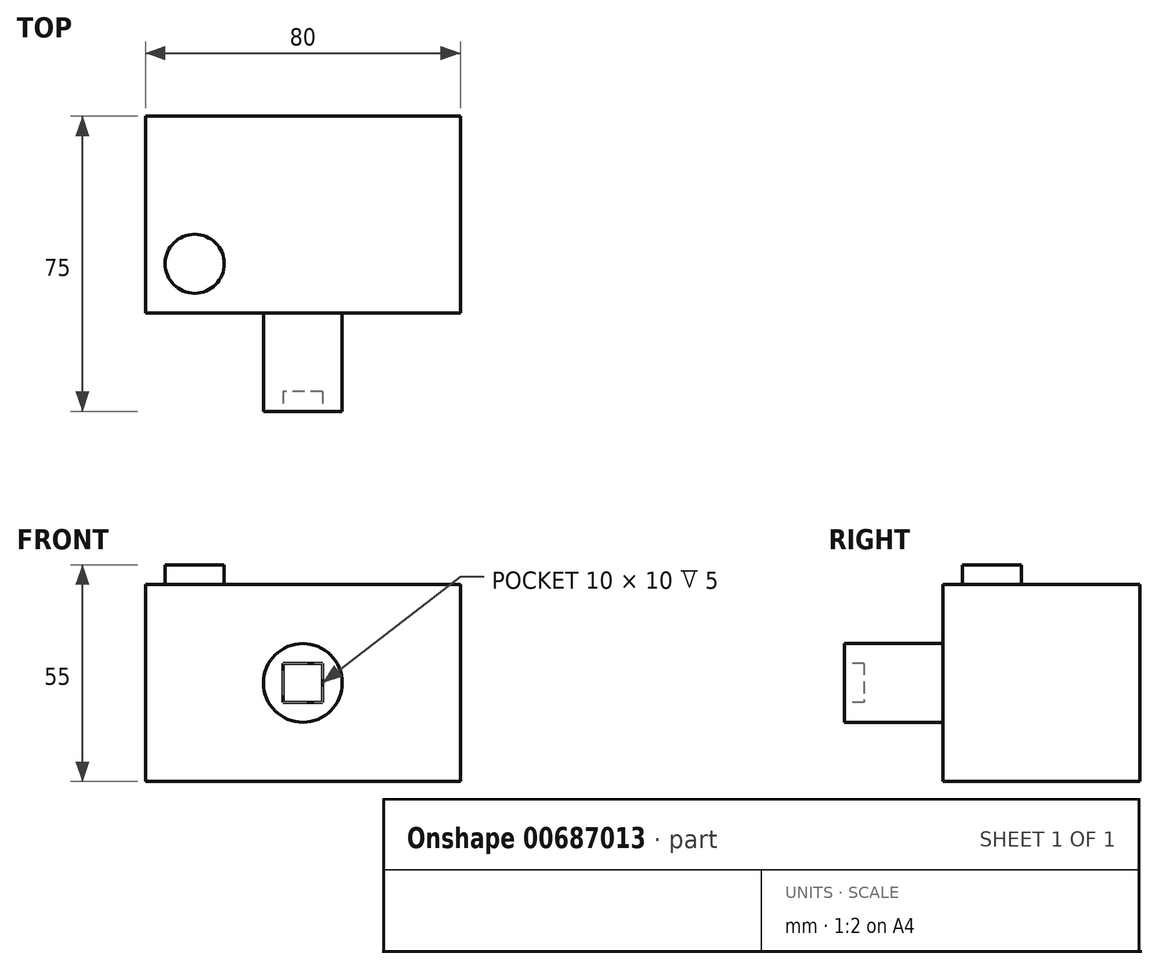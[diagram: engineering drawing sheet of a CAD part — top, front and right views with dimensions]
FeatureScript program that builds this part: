
annotation { "Feature Type Name" : "Feature", "Feature Type Description" : "" }
export const myFeature = defineFeature(function(context is Context, id is Id, definition is map)
    precondition{}
    {
        {
            var Q0;
            Q0=qCreatedBy(makeId("Top.planeOp"),FACE);
            var sketch = newSketch(context, id + "F0", { "sketchPlane" : qUnion([Q0])});
            skLineSegment(sketch, "E0.bottom", {"start": v(40, 25) * mm, "end": v(-40, 25) * mm});
            skLineSegment(sketch, "E0.top", {"start": v(40, -25) * mm, "end": v(-40, -25) * mm});
            skLineSegment(sketch, "E0.left", {"start": v(40, 25) * mm, "end": v(40, -25) * mm});
            skLineSegment(sketch, "E0.right", {"start": v(-40, 25) * mm, "end": v(-40, -25) * mm});
            skPoint(sketch, "E0.middle", {"position": v(0, 0) * mm});
            skSolve(sketch);
        }
        {
            var Q0;
            Q0 = qSketchRegion(id + "F0", true);
            extrude(context, id + "F1", {"entities" : qUnion([Q0]), "depth" : 50 * mm, "offsetDistance" : 25 * mm});
        }
        {
            var Q0;
            Q0=makeQuery(id+"F1.opExtrude","SWEPT_FACE",FACE,{"disambiguationData":[OSD([sQuery(id+"F0.wireOp",EDGE,"E0.top")])]});
            var sketch = newSketch(context, id + "F2", { "sketchPlane" : qUnion([Q0])});
            skCircle(sketch, "E1", {"center": v(0, 25) * mm, "radius": 10 * mm});
            skSolve(sketch);
        }
        {
            var Q0;
            Q0 = qSketchRegion(id + "F2", true);
            extrude(context, id + "F3", {"entities" : qUnion([Q0]), "operationType" : NewBodyOperationType.ADD, "depth" : 25 * mm, "offsetDistance" : 25 * mm});
        }
        {
            var Q0;
            Q0=makeQuery(id+"F3.opExtrude","CAP_FACE",FACE,{"disambiguationData":[OSD([sQuery(id+"F2.wireOp",EDGE,"E1")])],"isStart":false});
            var sketch = newSketch(context, id + "F4", { "sketchPlane" : qUnion([Q0])});
            skLineSegment(sketch, "E2.bottom", {"start": v(5, 30) * mm, "end": v(-5, 30) * mm});
            skLineSegment(sketch, "E2.top", {"start": v(5, 20) * mm, "end": v(-5, 20) * mm});
            skLineSegment(sketch, "E2.left", {"start": v(5, 30) * mm, "end": v(5, 20) * mm});
            skLineSegment(sketch, "E2.right", {"start": v(-5, 30) * mm, "end": v(-5, 20) * mm});
            skPoint(sketch, "E2.middle", {"position": v(0, 25) * mm});
            skSolve(sketch);
        }
        {
            var Q0;
            Q0 = qSketchRegion(id + "F4", true);
            extrude(context, id + "F5", {"entities" : qUnion([Q0]), "operationType" : NewBodyOperationType.REMOVE, "oppositeDirection" : true, "depth" : 5 * mm, "offsetDistance" : 25 * mm});
        }
        {
            var Q0;
            Q0=makeQuery(id+"F1.opExtrude","CAP_FACE",FACE,{"disambiguationData":[OSD([sQuery(id+"F0.wireOp",EDGE,"E0.bottom"),sQuery(id+"F0.wireOp",EDGE,"E0.top"),sQuery(id+"F0.wireOp",EDGE,"E0.left"),sQuery(id+"F0.wireOp",EDGE,"E0.right")])],"isStart":false});
            var sketch = newSketch(context, id + "F6", { "sketchPlane" : qUnion([Q0])});
            skCircle(sketch, "E3", {"center": v(-27.5, -12.5) * mm, "radius": 7.5 * mm});
            skSolve(sketch);
        }
        {
            var Q0;
            Q0 = qSketchRegion(id + "F6", true);
            extrude(context, id + "F7", {"entities" : qUnion([Q0]), "operationType" : NewBodyOperationType.ADD, "depth" : 5 * mm, "offsetDistance" : 25 * mm});
        }
    });
